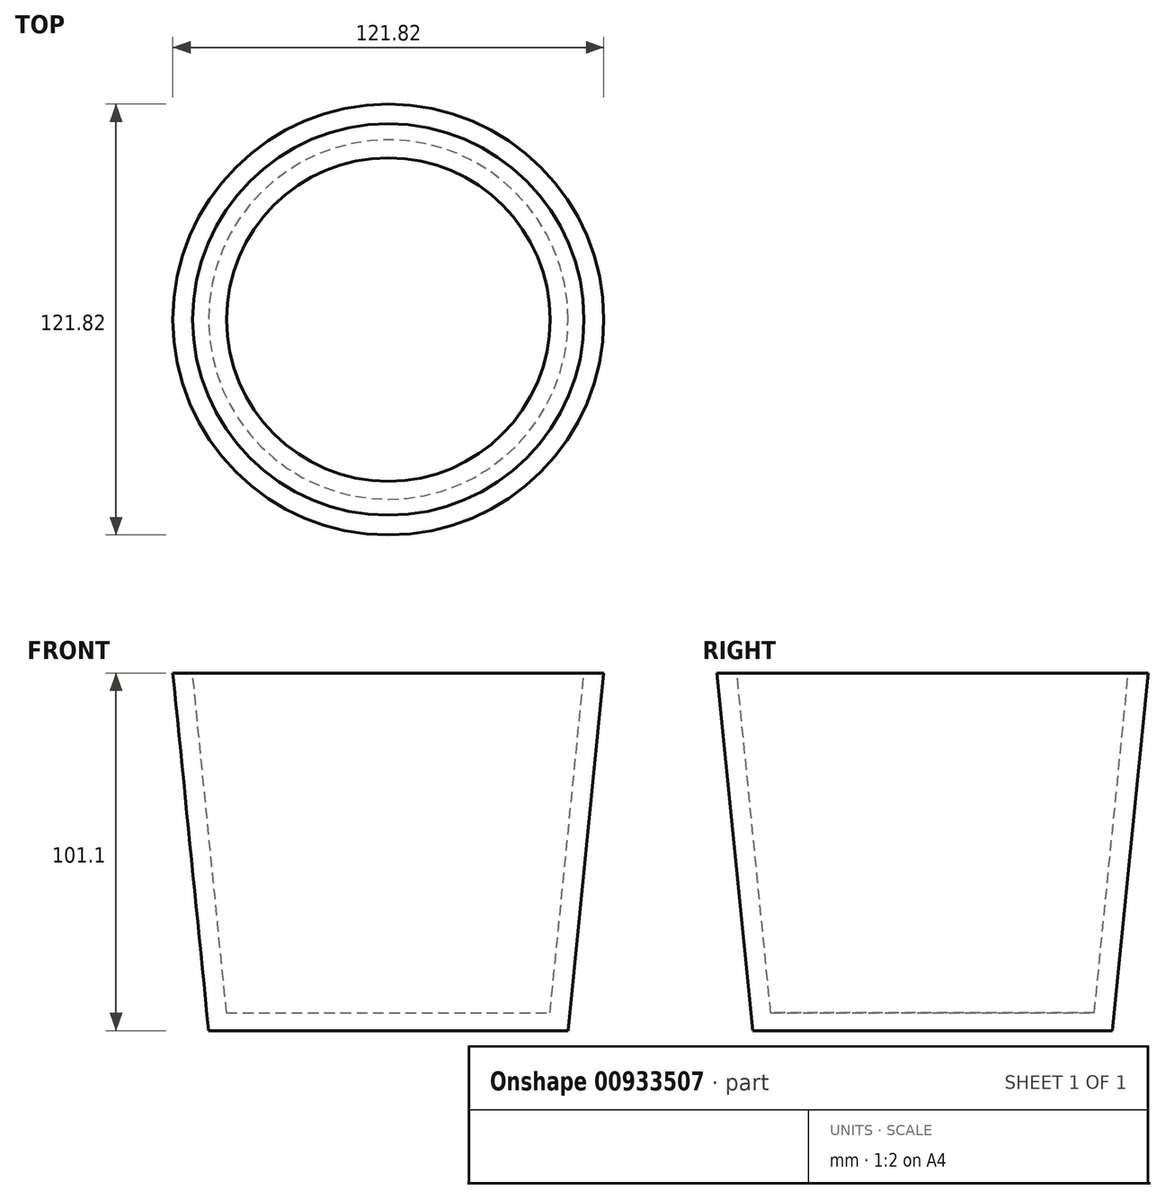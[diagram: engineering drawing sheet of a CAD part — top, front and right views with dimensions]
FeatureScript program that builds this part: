
annotation { "Feature Type Name" : "Feature", "Feature Type Description" : "" }
export const myFeature = defineFeature(function(context is Context, id is Id, definition is map)
    precondition{}
    {
        {
            var Q0;
            Q0=qCreatedBy(makeId("Front.planeOp"),FACE);
            var sketch = newSketch(context, id + "F0", { "sketchPlane" : qUnion([Q0])});
            skLineSegment(sketch, "E0", {"start": v(-60.9, 101.1) * mm, "end": v(-50.8, 0) * mm});
            skLineSegment(sketch, "E1", {"start": v(-60.9, 101.1) * mm, "end": v(-55.32, 101.1) * mm});
            skLineSegment(sketch, "E2", {"start": v(-55.32, 101.1) * mm, "end": v(-45.72, 5.08) * mm});
            skLineSegment(sketch, "E3", {"start": v(0, 0) * mm, "end": v(-50.8, 0) * mm});
            skLineSegment(sketch, "E4", {"start": v(-45.72, 5.08) * mm, "end": v(0, 5.08) * mm});
            skLineSegment(sketch, "E5", {"start": v(0, 0) * mm, "end": v(0, 5.08) * mm});
            skSolve(sketch);
        }
        {
            var Q0;
            Q0=makeQuery(id+"F0.imprint","IMPRINT",FACE,{"disambiguationData":[TD([[makeQuery(id+"F0.imprint","IMPRINT",EDGE,{"derivedFrom":sQuery(id+"F0.wireOp",EDGE,"E0")}),1.0]])]});
            var Q1;
            Q1=sQuery(id+"F0.wireOp",EDGE,"E5");
            revolve(context, id + "F1", {"surfaceOperationType" : NewSurfaceOperationType.NEW, "entities" : qUnion([Q0]), "axis" : qUnion([Q1]), "revolveType" : RevolveType.FULL});
        }
    });
